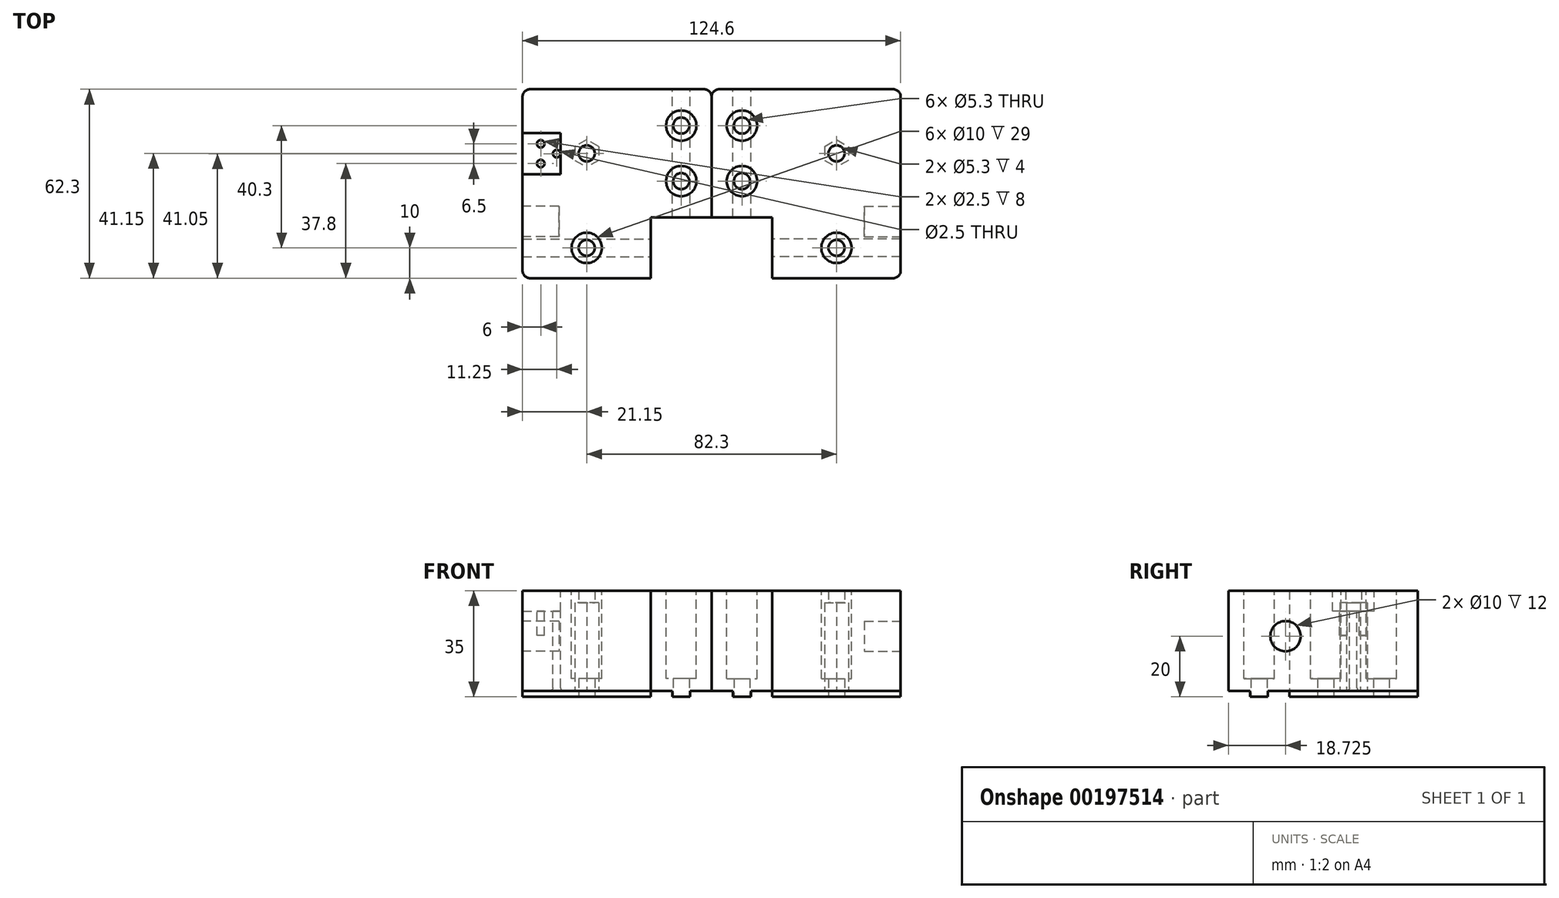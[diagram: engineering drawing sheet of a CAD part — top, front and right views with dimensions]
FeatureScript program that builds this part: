
annotation { "Feature Type Name" : "Feature", "Feature Type Description" : "" }
export const myFeature = defineFeature(function(context is Context, id is Id, definition is map)
    precondition{}
    {
        {
            var Q0;
            Q0=qCreatedBy(makeId("Top.planeOp"),FACE);
            var sketch = newSketch(context, id + "F0", { "sketchPlane" : qUnion([Q0])});
            skLineSegment(sketch, "E0.bottom", {"start": v(-21.15, 35) * mm, "end": v(41.15, 35) * mm});
            skLineSegment(sketch, "E0.top", {"start": v(-21.15, -27.3) * mm, "end": v(21.15, -27.3) * mm});
            skLineSegment(sketch, "E0.left", {"start": v(-21.15, 35) * mm, "end": v(-21.15, -27.3) * mm});
            skLineSegment(sketch, "E0.right", {"start": v(41.15, 35) * mm, "end": v(41.15, -7.3) * mm});
            skLineSegment(sketch, "E1.top", {"start": v(41.15, -7.3) * mm, "end": v(21.15, -7.3) * mm});
            skLineSegment(sketch, "E1.right", {"start": v(21.15, -27.3) * mm, "end": v(21.15, -7.3) * mm});
            skCircle(sketch, "E2", {"center": v(31.15, 23) * mm, "radius": 2.65 * mm});
            skCircle(sketch, "E3", {"center": v(31.15, 4.7) * mm, "radius": 2.65 * mm});
            skCircle(sketch, "E4", {"center": v(0, -17.3) * mm, "radius": 2.65 * mm});
            skPoint(sketch, "E4.centerSnap0", {"position": v(0, -27.3) * mm});
            skCircle(sketch, "E5", {"center": v(0, 13.85) * mm, "radius": 2.65 * mm});
            skSolve(sketch);
        }
        {
            var Q0;
            Q0=qSketchRegion(id+"F0",true);
            extrude(context, id + "F1", {"entities" : qUnion([Q0]), "depth" : 33 * mm});
        }
        {
            var Q0;
            Q0=makeQuery(id+"F1.opExtrude","SWEPT_FACE",FACE,{"disambiguationData":[OSD([sQuery(id+"F0.wireOp",EDGE,"E0.left")])]});
            var sketch = newSketch(context, id + "F2", { "sketchPlane" : qUnion([Q0])});
            skCircle(sketch, "E6", {"center": v(8.58, 18) * mm, "radius": 5 * mm});
            skSolve(sketch);
        }
        {
            var Q0;
            Q0=qSketchRegion(id+"F2",true);
            extrude(context, id + "F3", {"entities" : qUnion([Q0]), "operationType" : NewBodyOperationType.REMOVE, "oppositeDirection" : true, "depth" : 12 * mm});
        }
        {
            var Q0;
            Q0=makeQuery(id+"F1.opExtrude","CAP_FACE",FACE,{"disambiguationData":[OSD([sQuery(id+"F0.wireOp",EDGE,"E0.bottom"),sQuery(id+"F0.wireOp",EDGE,"E0.top"),sQuery(id+"F0.wireOp",EDGE,"E0.left"),sQuery(id+"F0.wireOp",EDGE,"E0.right"),sQuery(id+"F0.wireOp",EDGE,"E1.top"),sQuery(id+"F0.wireOp",EDGE,"E1.right"),sQuery(id+"F0.wireOp",EDGE,"E2"),sQuery(id+"F0.wireOp",EDGE,"E3"),sQuery(id+"F0.wireOp",EDGE,"YSbFCtBf-OZUa-blBg-jqSk-ddDIdjAn90QF"),sQuery(id+"F0.wireOp",EDGE,"E4"),sQuery(id+"F0.wireOp",EDGE,"E5")])],"isStart":true});
            var sketch = newSketch(context, id + "F4", { "sketchPlane" : qUnion([Q0])});
            skCircle(sketch, "E7.0", {"center": v(0, -13.85) * mm, "radius": 2.65 * mm, "construction": true});
            skCircle(sketch, "E8", {"center": v(0, -13.85) * mm, "radius": 3.95 * mm, "construction": true});
            skLineSegment(sketch, "E9", {"start": v(0, -20.58) * mm, "end": v(0, -4.16) * mm, "construction": true});
            skLineSegment(sketch, "E10", {"start": v(-6.74, -13.85) * mm, "end": v(6.1, -13.85) * mm, "construction": true});
            skLineSegment(sketch, "E11", {"start": v(-3.95, -16.13) * mm, "end": v(-3.95, -11.57) * mm});
            skLineSegment(sketch, "E12", {"start": v(-3.95, -11.57) * mm, "end": v(0, -9.29) * mm});
            skLineSegment(sketch, "E13", {"start": v(3.95, -16.13) * mm, "end": v(0, -18.41) * mm});
            skLineSegment(sketch, "E14", {"start": v(0, -18.41) * mm, "end": v(-3.95, -16.13) * mm});
            skLineSegment(sketch, "E15", {"start": v(3.95, -16.13) * mm, "end": v(3.95, -11.57) * mm});
            skLineSegment(sketch, "E16", {"start": v(3.95, -11.57) * mm, "end": v(0, -9.29) * mm});
            skSolve(sketch);
        }
        {
            var Q0;
            Q0=qSketchRegion(id+"F4",true);
            extrude(context, id + "F5", {"entities" : qUnion([Q0]), "operationType" : NewBodyOperationType.REMOVE, "oppositeDirection" : true, "depth" : 29 * mm});
        }
        {
            var Q0;
            Q0=makeQuery(id+"F1.opExtrude","CAP_FACE",FACE,{"disambiguationData":[OSD([sQuery(id+"F0.wireOp",EDGE,"E0.bottom"),sQuery(id+"F0.wireOp",EDGE,"E0.top"),sQuery(id+"F0.wireOp",EDGE,"E0.left"),sQuery(id+"F0.wireOp",EDGE,"E0.right"),sQuery(id+"F0.wireOp",EDGE,"E1.top"),sQuery(id+"F0.wireOp",EDGE,"E1.right"),sQuery(id+"F0.wireOp",EDGE,"E2"),sQuery(id+"F0.wireOp",EDGE,"E3"),sQuery(id+"F0.wireOp",EDGE,"YSbFCtBf-OZUa-blBg-jqSk-ddDIdjAn90QF"),sQuery(id+"F0.wireOp",EDGE,"E4"),sQuery(id+"F0.wireOp",EDGE,"E5")])],"isStart":false});
            var sketch = newSketch(context, id + "F6", { "sketchPlane" : qUnion([Q0])});
            skCircle(sketch, "E17.0", {"center": v(31.15, 23) * mm, "radius": 2.65 * mm, "construction": true});
            skCircle(sketch, "E18.0", {"center": v(31.15, 4.7) * mm, "radius": 2.65 * mm, "construction": true});
            skCircle(sketch, "E19.0", {"center": v(0, -17.3) * mm, "radius": 2.65 * mm, "construction": true});
            skCircle(sketch, "E20", {"center": v(31.15, 23) * mm, "radius": 5 * mm});
            skCircle(sketch, "E21", {"center": v(31.15, 4.7) * mm, "radius": 5 * mm});
            skCircle(sketch, "E22", {"center": v(0, -17.3) * mm, "radius": 5 * mm});
            skSolve(sketch);
        }
        {
            var Q0;
            Q0=qSketchRegion(id+"F6",true);
            extrude(context, id + "F7", {"entities" : qUnion([Q0]), "operationType" : NewBodyOperationType.REMOVE, "oppositeDirection" : true, "depth" : 29 * mm});
        }
        {
            var Q0;
            Q0=makeQuery(id+"F1.opExtrude","SWEPT_EDGE",EDGE,{"disambiguationData":[OSD([sQuery(id+"F0.wireOp",EDGE,"E0.top"),sQuery(id+"F0.wireOp",EDGE,"E0.left")])]});
            var Q1;
            Q1=makeQuery(id+"F1.opExtrude","SWEPT_EDGE",EDGE,{"disambiguationData":[OSD([sQuery(id+"F0.wireOp",EDGE,"E0.bottom"),sQuery(id+"F0.wireOp",EDGE,"E0.left")])]});
            var Q2;
            Q2=makeQuery(id+"F1.opExtrude","SWEPT_EDGE",EDGE,{"disambiguationData":[OSD([sQuery(id+"F0.wireOp",EDGE,"E0.bottom"),sQuery(id+"F0.wireOp",EDGE,"E0.right")])]});
            fillet(context, id + "F8", {"entities" : qUnion([Q0, Q1, Q2]), "radius" : 2.5 * mm, "tangentPropagation" : true, "allowEdgeOverflow" : false});
        }
        {
            var Q0;
            Q0=makeQuery(id+"F1.opExtrude","CAP_FACE",FACE,{"disambiguationData":[OSD([sQuery(id+"F0.wireOp",EDGE,"E0.bottom"),sQuery(id+"F0.wireOp",EDGE,"E0.top"),sQuery(id+"F0.wireOp",EDGE,"E0.left"),sQuery(id+"F0.wireOp",EDGE,"E0.right"),sQuery(id+"F0.wireOp",EDGE,"E1.top"),sQuery(id+"F0.wireOp",EDGE,"E1.right"),sQuery(id+"F0.wireOp",EDGE,"E2"),sQuery(id+"F0.wireOp",EDGE,"E3"),sQuery(id+"F0.wireOp",EDGE,"YSbFCtBf-OZUa-blBg-jqSk-ddDIdjAn90QF"),sQuery(id+"F0.wireOp",EDGE,"E4"),sQuery(id+"F0.wireOp",EDGE,"E5")])],"isStart":true});
            var sketch = newSketch(context, id + "F9", { "sketchPlane" : qUnion([Q0])});
            skLineSegment(sketch, "E23.bottom", {"start": v(28.2, 7.3) * mm, "end": v(34.1, 7.3) * mm});
            skLineSegment(sketch, "E23.top", {"start": v(28.2, -35) * mm, "end": v(34.1, -35) * mm});
            skLineSegment(sketch, "E23.left", {"start": v(28.2, 7.3) * mm, "end": v(28.2, -13.57) * mm});
            skLineSegment(sketch, "E23.right", {"start": v(34.1, 7.3) * mm, "end": v(34.1, -13.57) * mm});
            skCircle(sketch, "E24.0", {"center": v(31.15, -4.7) * mm, "radius": 2.65 * mm});
            skCircle(sketch, "E25.0", {"center": v(31.15, -23) * mm, "radius": 2.65 * mm});
            skLineSegment(sketch, "E26.trimOffspring", {"start": v(28.2, -13.57) * mm, "end": v(28.2, -35) * mm});
            skLineSegment(sketch, "E27.trimOffspring", {"start": v(34.1, -13.57) * mm, "end": v(34.1, -35) * mm});
            skLineSegment(sketch, "E28.bottom", {"start": v(-21.15, 20.25) * mm, "end": v(21.15, 20.25) * mm});
            skLineSegment(sketch, "E28.top", {"start": v(-21.15, 14.35) * mm, "end": v(21.15, 14.35) * mm});
            skLineSegment(sketch, "E28.left", {"start": v(-21.15, 20.25) * mm, "end": v(-21.15, 14.35) * mm});
            skLineSegment(sketch, "E28.right", {"start": v(21.15, 20.25) * mm, "end": v(21.15, 14.35) * mm});
            skCircle(sketch, "E29.0", {"center": v(0, 17.3) * mm, "radius": 2.65 * mm});
            skSolve(sketch);
        }
        {
            var Q0;
            Q0=qSketchRegion(id+"F9",true);
            extrude(context, id + "F10", {"entities" : qUnion([Q0]), "operationType" : NewBodyOperationType.ADD, "depth" : 2 * mm});
        }
        {
            var Q0;
            Q0=makeQuery(id+"F1.opExtrude","SWEPT_BODY",BODY,{"disambiguationData":[OSD([sQuery(id+"F0.wireOp",EDGE,"E0.bottom"),sQuery(id+"F0.wireOp",EDGE,"E0.top"),sQuery(id+"F0.wireOp",EDGE,"E0.left"),sQuery(id+"F0.wireOp",EDGE,"E0.right"),sQuery(id+"F0.wireOp",EDGE,"E1.top"),sQuery(id+"F0.wireOp",EDGE,"E1.right"),sQuery(id+"F0.wireOp",EDGE,"E2"),sQuery(id+"F0.wireOp",EDGE,"E3"),sQuery(id+"F0.wireOp",EDGE,"YSbFCtBf-OZUa-blBg-jqSk-ddDIdjAn90QF"),sQuery(id+"F0.wireOp",EDGE,"E4"),sQuery(id+"F0.wireOp",EDGE,"E5")])]});
            var Q1;
            Q1=makeQuery(id+"F1.opExtrude","SWEPT_FACE",FACE,{"disambiguationData":[OSD([sQuery(id+"F0.wireOp",EDGE,"E0.right")])]});
            mirror(context, id + "F11", {"entities" : qUnion([Q0]), "mirrorPlane" : qUnion([Q1])});
        }
        {
            var Q0;
            Q0=makeQuery(id+"F1.opExtrude","CAP_FACE",FACE,{"disambiguationData":[OSD([sQuery(id+"F0.wireOp",EDGE,"E0.bottom"),sQuery(id+"F0.wireOp",EDGE,"E0.top"),sQuery(id+"F0.wireOp",EDGE,"E0.left"),sQuery(id+"F0.wireOp",EDGE,"E0.right"),sQuery(id+"F0.wireOp",EDGE,"E1.top"),sQuery(id+"F0.wireOp",EDGE,"E1.right"),sQuery(id+"F0.wireOp",EDGE,"E2"),sQuery(id+"F0.wireOp",EDGE,"E3"),sQuery(id+"F0.wireOp",EDGE,"E4"),sQuery(id+"F0.wireOp",EDGE,"E5")])],"isStart":false});
            var sketch = newSketch(context, id + "F12", { "sketchPlane" : qUnion([Q0])});
            skLineSegment(sketch, "E30.bottom", {"start": v(-21.15, 20.6) * mm, "end": v(-13.65, 20.6) * mm});
            skLineSegment(sketch, "E30.top", {"start": v(-21.15, 6.9) * mm, "end": v(-13.65, 6.9) * mm});
            skLineSegment(sketch, "E30.left", {"start": v(-21.15, 20.6) * mm, "end": v(-21.15, 6.9) * mm});
            skLineSegment(sketch, "E30.right", {"start": v(-13.65, 20.6) * mm, "end": v(-13.65, 6.9) * mm});
            skLineSegment(sketch, "E31.bottom", {"start": v(-13.65, 20.6) * mm, "end": v(-8.65, 20.6) * mm});
            skLineSegment(sketch, "E31.top", {"start": v(-13.65, 6.9) * mm, "end": v(-8.65, 6.9) * mm});
            skLineSegment(sketch, "E31.left", {"start": v(-13.65, 20.6) * mm, "end": v(-13.65, 6.9) * mm, "construction": true});
            skLineSegment(sketch, "E31.right", {"start": v(-8.65, 20.6) * mm, "end": v(-8.65, 6.9) * mm});
            skSolve(sketch);
        }
        {
            var Q0;
            Q0=qSketchRegion(id+"F12",true);
            extrude(context, id + "F13", {"entities" : qUnion([Q0]), "operationType" : NewBodyOperationType.REMOVE, "oppositeDirection" : true, "depth" : 6.8 * mm});
        }
        {
            var Q0;
            Q0=makeQuery(id+"F13.boolean.opBoolean","COPY",FACE,{"derivedFrom":makeQuery(id+"F13.opExtrude","CAP_FACE",FACE,{"disambiguationData":[OSD([sQuery(id+"F12.wireOp",EDGE,"E30.bottom"),sQuery(id+"F12.wireOp",EDGE,"E30.top"),sQuery(id+"F12.wireOp",EDGE,"E30.left"),sQuery(id+"F12.wireOp",EDGE,"E30.right")])],"isStart":false})});
            var sketch = newSketch(context, id + "F14", { "sketchPlane" : qUnion([Q0])});
            skCircle(sketch, "E32", {"center": v(-15.15, 17) * mm, "radius": 1.25 * mm});
            skCircle(sketch, "E33", {"center": v(-15.15, 10.5) * mm, "radius": 1.25 * mm});
            skSolve(sketch);
        }
        {
            var Q0;
            Q0=qSketchRegion(id+"F14",true);
            extrude(context, id + "F15", {"entities" : qUnion([Q0]), "operationType" : NewBodyOperationType.REMOVE, "oppositeDirection" : true, "depth" : 8 * mm});
        }
        {
            var Q0;
            Q0=makeQuery(id+"F13.boolean.opBoolean","COPY",FACE,{"derivedFrom":makeQuery(id+"F13.opExtrude","CAP_FACE",FACE,{"disambiguationData":[OSD([sQuery(id+"F12.wireOp",EDGE,"E30.bottom"),sQuery(id+"F12.wireOp",EDGE,"E30.top"),sQuery(id+"F12.wireOp",EDGE,"E30.left"),sQuery(id+"F12.wireOp",EDGE,"E31.bottom"),sQuery(id+"F12.wireOp",EDGE,"E31.top"),sQuery(id+"F12.wireOp",EDGE,"E31.right")])],"isStart":false})});
            var sketch = newSketch(context, id + "F16", { "sketchPlane" : qUnion([Q0])});
            skCircle(sketch, "E34", {"center": v(-9.9, 13.75) * mm, "radius": 1.25 * mm});
            skPoint(sketch, "E34.centerSnap0", {"position": v(-8.65, 13.75) * mm});
            skSolve(sketch);
        }
        {
            var Q0;
            Q0=qSketchRegion(id+"F16",true);
            extrude(context, id + "F17", {"entities" : qUnion([Q0]), "operationType" : NewBodyOperationType.REMOVE, "oppositeDirection" : true, "depth" : 30 * mm});
        }
        {
            var Q0;
            Q0=makeQuery(id+"F17.boolean.opBoolean","COPY",EDGE,{"derivedFrom":makeQuery(id+"F17.opExtrude","CAP_EDGE",EDGE,{"disambiguationData":[OSD([sQuery(id+"F16.wireOp",EDGE,"E34")])],"isStart":true})});
            var Q1;
            {var subQ0=sQuery(id+"F0.wireOp",EDGE,"E0.bottom");var subQ1=sQuery(id+"F0.wireOp",EDGE,"E0.left");var subQ2=sQuery(id+"F0.wireOp",EDGE,"E1.right");var subQ3=sQuery(id+"F0.wireOp",EDGE,"E1.top");Q1=makeQuery(id+"F17.boolean.opBoolean","INTERSECT",EDGE,{"derivedFrom":[makeQuery(id+"F10.boolean.opBoolean","SPLIT",FACE,{"disambiguationData":[TD([makeQuery(id+"F5.boolean.opBoolean","COPY",FACE,{"derivedFrom":makeQuery(id+"F5.opExtrude","SWEPT_FACE",FACE,{"disambiguationData":[OSD([sQuery(id+"F4.wireOp",EDGE,"E11")])]})})])],"derivedFrom":makeQuery(id+"F1.opExtrude","CAP_FACE",FACE,{"disambiguationData":[OSD([subQ0,sQuery(id+"F0.wireOp",EDGE,"E0.top"),subQ1,sQuery(id+"F0.wireOp",EDGE,"E0.right"),subQ3,subQ2,sQuery(id+"F0.wireOp",EDGE,"E2"),sQuery(id+"F0.wireOp",EDGE,"E3"),sQuery(id+"F0.wireOp",EDGE,"E4"),sQuery(id+"F0.wireOp",EDGE,"E5")])],"isStart":true})}),makeQuery(id+"F17.opExtrude","SWEPT_FACE",FACE,{"disambiguationData":[OSD([sQuery(id+"F16.wireOp",EDGE,"E34")])]})]});}
            fillet(context, id + "F18", {"entities" : qUnion([Q0, Q1]), "radius" : 1 * mm, "tangentPropagation" : true, "allowEdgeOverflow" : false});
        }
    });
